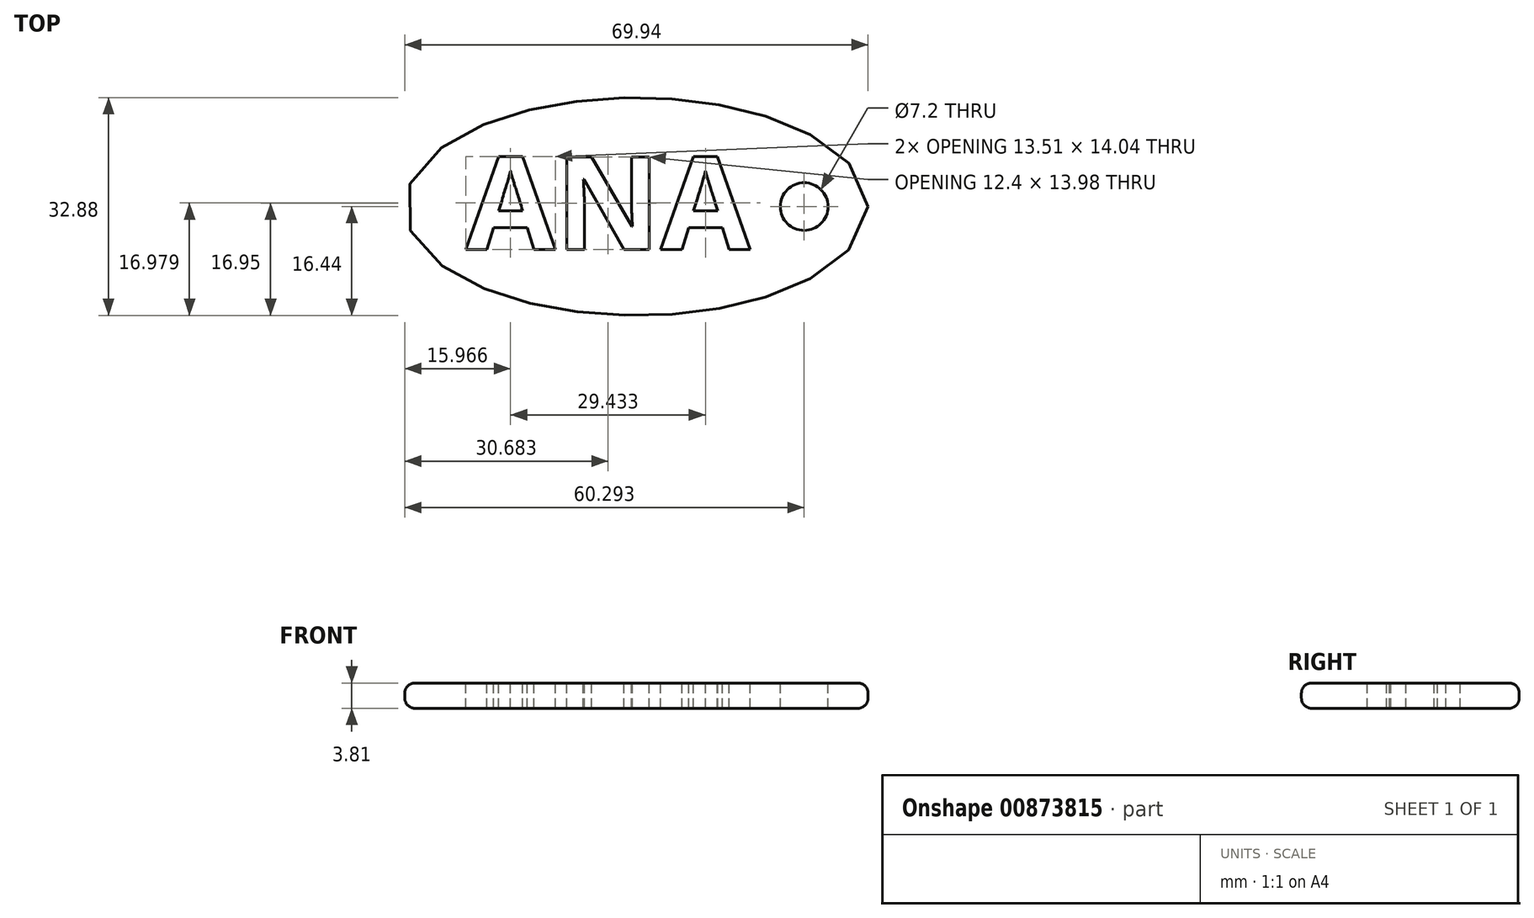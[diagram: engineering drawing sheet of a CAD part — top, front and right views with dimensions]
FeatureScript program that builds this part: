
annotation { "Feature Type Name" : "Feature", "Feature Type Description" : "" }
export const myFeature = defineFeature(function(context is Context, id is Id, definition is map)
    precondition{}
    {
        {
            var Q0;
            Q0=qCreatedBy(makeId("Top.planeOp"),FACE);
            var sketch = newSketch(context, id + "F0", { "sketchPlane" : qUnion([Q0])});
            skEllipse(sketch, "E0", {"center": v(0, 0) * mm, "majorRadius": 34.97 * mm, "minorRadius": 16.44 * mm, "majorAxis": v(1, 0)});
            skSolve(sketch);
        }
        {
            var Q0;
            Q0 = qSketchRegion(id + "F0", true);
            extrude(context, id + "F1", {"entities" : qUnion([Q0]), "depth" : 3.8 * mm, "offsetDistance" : 25.4 * mm});
        }
        {
            var Q0;
            Q0=makeQuery(id+"F1.opExtrude","CAP_FACE",FACE,{"disambiguationData":[OSD([sQuery(id+"F0.wireOp",EDGE,"E0")])],"isStart":false});
            var Q1;
            Q1=makeQuery(id+"F1.opExtrude","CAP_FACE",FACE,{"disambiguationData":[OSD([sQuery(id+"F0.wireOp",EDGE,"E0")])],"isStart":true});
            fillet(context, id + "F2", {"entities" : qUnion([Q0, Q1]), "radius" : 1.52 * mm, "tangentPropagation" : true, "allowEdgeOverflow" : false});
        }
        {
            var Q0;
            Q0=makeQuery(id+"F1.opExtrude","CAP_FACE",FACE,{"disambiguationData":[OSD([sQuery(id+"F0.wireOp",EDGE,"E0")])],"isStart":false});
            var sketch = newSketch(context, id + "F3", { "sketchPlane" : qUnion([Q0])});
            skText(sketch, "E1", { "text": "ANA", "fontName": "OpenSans-Bold.ttf"});
            skCircle(sketch, "E2", {"center": v(25.32, 0) * mm, "radius": 3.6 * mm});
            const initialGuessF3  = {"E1": [-0.02576, -0.00648, 1, 0, 0.0141]};
            skSetInitialGuess(sketch, initialGuessF3);
            skSolve(sketch);
        }
        {
            var Q0;
            Q0 = qSketchRegion(id + "F3", true);
            extrude(context, id + "F4", {"entities" : qUnion([Q0]), "operationType" : NewBodyOperationType.REMOVE, "endBound" : BoundingType.THROUGH_ALL, "oppositeDirection" : true, "depth" : 25.4 * mm, "offsetDistance" : 25.4 * mm});
        }
    });
